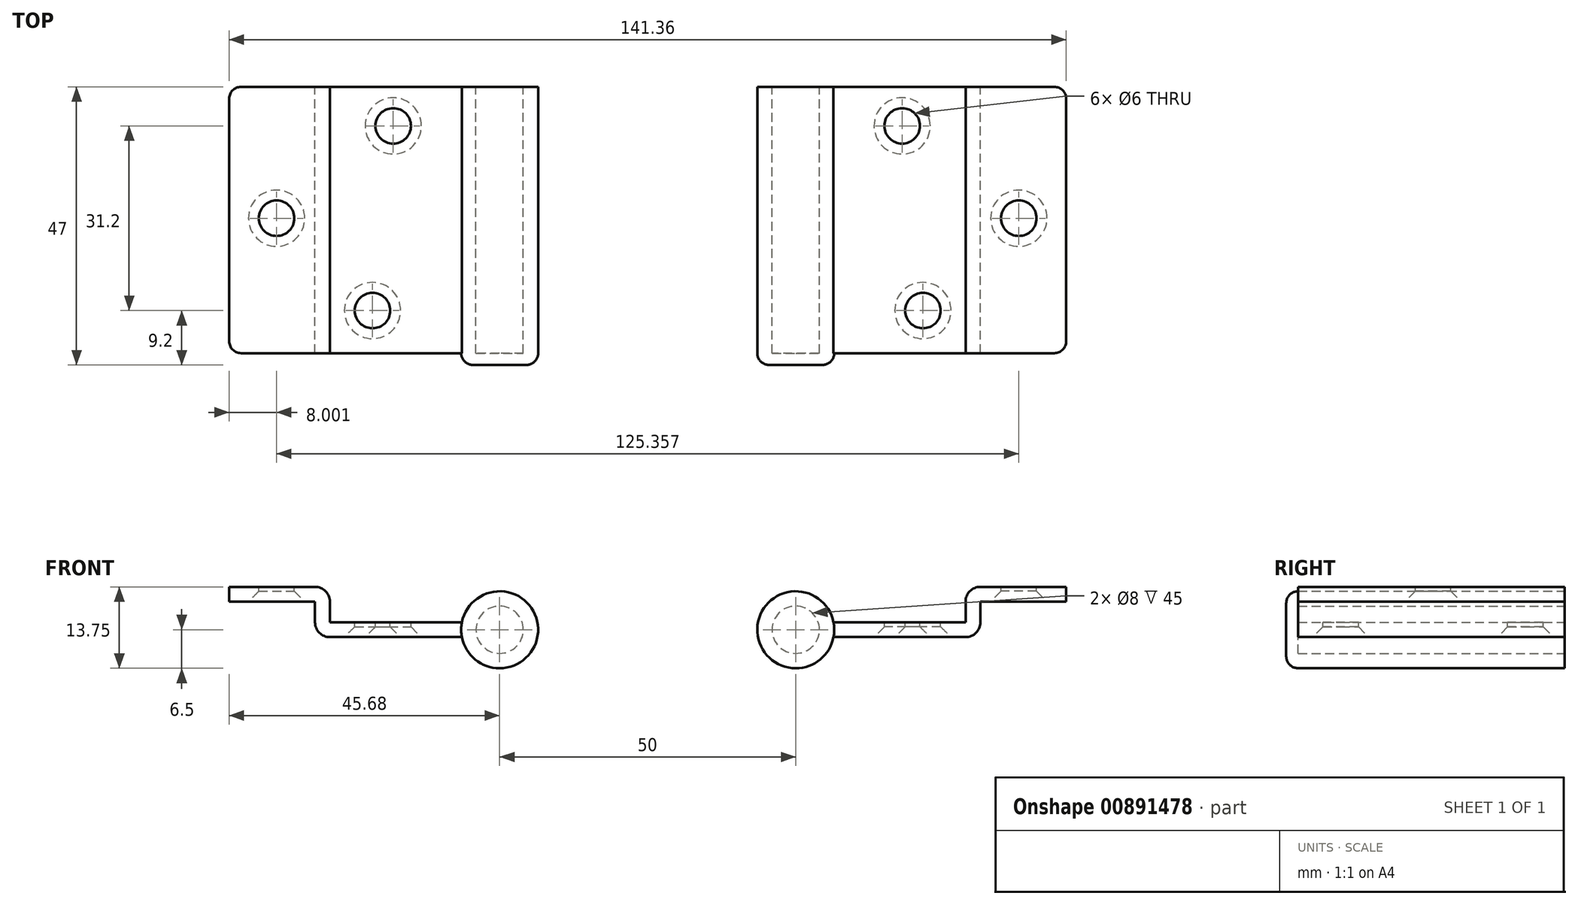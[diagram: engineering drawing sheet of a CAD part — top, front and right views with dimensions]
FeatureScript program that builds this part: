
annotation { "Feature Type Name" : "Feature", "Feature Type Description" : "" }
export const myFeature = defineFeature(function(context is Context, id is Id, definition is map)
    precondition{}
    {
        {
            var Q0;
            Q0=qCreatedBy(makeId("Front.planeOp"),FACE);
            var sketch = newSketch(context, id + "F0", { "sketchPlane" : qUnion([Q0])});
            skArc(sketch, "E0", {"start": v(6.38, 1.25) * mm, "mid": v(-6.5, 0) * mm, "end": v(6.38, -1.25) * mm});
            skLineSegment(sketch, "E1", {"start": v(6.38, 1.25) * mm, "end": v(28.68, 1.25) * mm});
            skLineSegment(sketch, "E2", {"start": v(28.68, 7.25) * mm, "end": v(45.68, 7.25) * mm});
            skLineSegment(sketch, "E3", {"start": v(45.68, 7.25) * mm, "end": v(45.68, 4.75) * mm});
            skLineSegment(sketch, "E4", {"start": v(45.68, 4.75) * mm, "end": v(31.18, 4.75) * mm});
            skLineSegment(sketch, "E5", {"start": v(31.18, -1.25) * mm, "end": v(6.38, -1.25) * mm});
            skLineSegment(sketch, "E6", {"start": v(31.18, 4.75) * mm, "end": v(31.18, -1.25) * mm});
            skLineSegment(sketch, "E7", {"start": v(28.68, 7.25) * mm, "end": v(28.68, 1.25) * mm});
            skCircle(sketch, "E8", {"center": v(0, 0) * mm, "radius": 4 * mm});
            skSolve(sketch);
        }
        {
            var Q0;
            Q0=makeQuery(id+"F0.imprint","IMPRINT",FACE,{"disambiguationData":[TD([[makeQuery(id+"F0.imprint","IMPRINT",EDGE,{"derivedFrom":sQuery(id+"F0.wireOp",EDGE,"E0")}),1.0]])]});
            extrude(context, id + "F1", {"entities" : qUnion([Q0]), "depth" : 45 * mm, "offsetDistance" : 25 * mm});
        }
        {
            var Q0;
            Q0=makeQuery(id+"F1.opExtrude","CAP_EDGE",EDGE,{"disambiguationData":[OSD([sQuery(id+"F0.wireOp",EDGE,"E3")])],"isStart":false});
            var Q1;
            Q1=makeQuery(id+"F1.opExtrude","CAP_EDGE",EDGE,{"disambiguationData":[OSD([sQuery(id+"F0.wireOp",EDGE,"E3")])],"isStart":true});
            fillet(context, id + "F2", {"entities" : qUnion([Q0, Q1]), "radius" : 2 * mm, "tangentPropagation" : true, "allowEdgeOverflow" : false});
        }
        {
            var Q0;
            Q0=makeQuery(id+"F1.opExtrude","SWEPT_EDGE",EDGE,{"disambiguationData":[OSD([sQuery(id+"F0.wireOp",EDGE,"E5"),sQuery(id+"F0.wireOp",EDGE,"E6")])]});
            var Q1;
            Q1=makeQuery(id+"F1.opExtrude","SWEPT_EDGE",EDGE,{"disambiguationData":[OSD([sQuery(id+"F0.wireOp",EDGE,"E2"),sQuery(id+"F0.wireOp",EDGE,"E7")])]});
            fillet(context, id + "F3", {"entities" : qUnion([Q0, Q1]), "radius" : 2.5 * mm, "tangentPropagation" : true, "allowEdgeOverflow" : false});
        }
        {
            var Q0;
            Q0=makeQuery(id+"F1.opExtrude","SWEPT_FACE",FACE,{"disambiguationData":[OSD([sQuery(id+"F0.wireOp",EDGE,"E5")])]});
            var sketch = newSketch(context, id + "F4", { "sketchPlane" : qUnion([Q0])});
            skPoint(sketch, "E9", {"position": v(17.98, 6.6) * mm});
            skPoint(sketch, "E10", {"position": v(21.48, 37.8) * mm});
            skSolve(sketch);
        }
        {
            var Q0;
            Q0=sQuery(id+"F4.wireOp",VERTEX,"E9");
            var Q1;
            Q1=sQuery(id+"F4.wireOp",VERTEX,"E10");
            var Q2;
            Q2=sQuery(id+"F1gnd5VNBVrkXNz_1.wireOp",VERTEX,"af38a646-69fc-4794-a32b-26258d2a7c5d");
            var Q3;
            Q3=makeQuery(id+"F1.opExtrude","SWEPT_BODY",BODY,{"disambiguationData":[OSD([sQuery(id+"F0.wireOp",EDGE,"E0"),sQuery(id+"F0.wireOp",EDGE,"E1"),sQuery(id+"F0.wireOp",EDGE,"WSlHtf5i-U6j4-Ynl4-FoHb-XjoWY4hGSOt6"),sQuery(id+"F0.wireOp",EDGE,"E2"),sQuery(id+"F0.wireOp",EDGE,"E3"),sQuery(id+"F0.wireOp",EDGE,"E4"),sQuery(id+"F0.wireOp",EDGE,"E5"),sQuery(id+"F0.wireOp",EDGE,"dJLKLTg6-jbDR-ftkV-erEf-zidkdKnkohMK"),sQuery(id+"F0.wireOp",EDGE,"M6QVCp6i-pHj4-OTcd-NfKp-MZP8uRFXvbLj"),sQuery(id+"F0.wireOp",EDGE,"RtBS60rh-hvOl-1zH0-KM05-FjQfmGGDyUj7")])]});
            hole(context, id + "F5", {"style" : HoleStyle.C_SINK, "endStyle" : HoleEndStyle.THROUGH, "standardTappedOrClearance" : lookupTablePath({ "standard" : "ISO", "size" : "6", "type" : "Drilled" }), "standardBlindInLast" : lookupTablePath({ "standard" : "ISO", "size" : "6", "type" : "Drilled" }), "holeDiameter" : 6 * mm, "cSinkDiameter" : 9.5 * mm, "cSinkAngle" : 90 * degree, "majorDiameter" : 5 * mm, "isTappedThrough" : true, "tappedDepth" : 12 * mm, "tapClearance" : 3, "startFromSketch" : true, "locations" : qUnion([Q0, Q1, Q2]), "scope" : qUnion([Q3])});
        }
        {
            var Q0;
            Q0=makeQuery(id+"F1.opExtrude","CAP_FACE",FACE,{"disambiguationData":[OSD([sQuery(id+"F0.wireOp",EDGE,"E0"),sQuery(id+"F0.wireOp",EDGE,"E1"),sQuery(id+"F0.wireOp",EDGE,"WSlHtf5i-U6j4-Ynl4-FoHb-XjoWY4hGSOt6"),sQuery(id+"F0.wireOp",EDGE,"E2"),sQuery(id+"F0.wireOp",EDGE,"E3"),sQuery(id+"F0.wireOp",EDGE,"E4"),sQuery(id+"F0.wireOp",EDGE,"E5"),sQuery(id+"F0.wireOp",EDGE,"dJLKLTg6-jbDR-ftkV-erEf-zidkdKnkohMK"),sQuery(id+"F0.wireOp",EDGE,"M6QVCp6i-pHj4-OTcd-NfKp-MZP8uRFXvbLj"),sQuery(id+"F0.wireOp",EDGE,"RtBS60rh-hvOl-1zH0-KM05-FjQfmGGDyUj7")])],"isStart":false});
            var sketch = newSketch(context, id + "F6", { "sketchPlane" : qUnion([Q0])});
            skCircle(sketch, "E11", {"center": v(0, 0) * mm, "radius": 6.5 * mm});
            skSolve(sketch);
        }
        {
            var Q0;
            Q0=qSketchRegion(id+"F6",true);
            extrude(context, id + "F7", {"entities" : qUnion([Q0]), "operationType" : NewBodyOperationType.ADD, "depth" : 2 * mm, "offsetDistance" : 25 * mm});
        }
        {
            var Q0;
            Q0=makeQuery(id+"F7.opExtrude","CAP_EDGE",EDGE,{"disambiguationData":[OSD([sQuery(id+"F6.wireOp",EDGE,"E11")])],"isStart":false});
            fillet(context, id + "F8", {"entities" : qUnion([Q0]), "radius" : 2 * mm, "tangentPropagation" : true, "allowEdgeOverflow" : false});
        }
        {
            var Q0;
            Q0=makeQuery(id+"F1.opExtrude","SWEPT_FACE",FACE,{"disambiguationData":[OSD([sQuery(id+"F0.wireOp",EDGE,"E4")])]});
            var sketch = newSketch(context, id + "F9", { "sketchPlane" : qUnion([Q0])});
            skPoint(sketch, "E12", {"position": v(37.68, 22.2) * mm});
            skLineSegment(sketch, "E13.bottom", {"start": v(28.68, 27.7) * mm, "end": v(33.68, 27.7) * mm});
            skLineSegment(sketch, "E13.top", {"start": v(28.68, 16.7) * mm, "end": v(33.68, 16.7) * mm});
            skLineSegment(sketch, "E13.left", {"start": v(28.68, 27.7) * mm, "end": v(28.68, 16.7) * mm});
            skLineSegment(sketch, "E13.right", {"start": v(33.68, 27.7) * mm, "end": v(33.68, 16.7) * mm});
            skPoint(sketch, "E13.middle", {"position": v(31.18, 22.2) * mm});
            skPoint(sketch, "E13.middle.positionSnap0", {"position": v(31.18, 22.5) * mm});
            skPoint(sketch, "E13.centerSnap0", {"position": v(31.18, 22.5) * mm});
            skSolve(sketch);
        }
        {
            var Q0;
            Q0=sQuery(id+"F9.wireOp",VERTEX,"E12");
            var Q1;
            Q1=makeQuery(id+"F1.opExtrude","SWEPT_BODY",BODY,{"disambiguationData":[OSD([sQuery(id+"F0.wireOp",EDGE,"E0"),sQuery(id+"F0.wireOp",EDGE,"E1"),sQuery(id+"F0.wireOp",EDGE,"E2"),sQuery(id+"F0.wireOp",EDGE,"E3"),sQuery(id+"F0.wireOp",EDGE,"E4"),sQuery(id+"F0.wireOp",EDGE,"E5"),sQuery(id+"F0.wireOp",EDGE,"E6"),sQuery(id+"F0.wireOp",EDGE,"E7")])]});
            hole(context, id + "F10", {"style" : HoleStyle.C_SINK, "endStyle" : HoleEndStyle.THROUGH, "standardTappedOrClearance" : lookupTablePath({ "standard" : "ISO", "size" : "6", "type" : "Drilled" }), "standardBlindInLast" : lookupTablePath({ "standard" : "ISO", "size" : "6", "type" : "Drilled" }), "holeDiameter" : 6 * mm, "cSinkDiameter" : 9.5 * mm, "cSinkAngle" : 90 * degree, "majorDiameter" : 5 * mm, "isTappedThrough" : true, "tappedDepth" : 12 * mm, "tapClearance" : 3, "startFromSketch" : true, "locations" : qUnion([Q0]), "scope" : qUnion([Q1])});
        }
        {
            var Q0;
            Q0=qCreatedBy(makeId("Right.planeOp"),FACE);
            cPlane(context, id + "F11", {"entities" : qUnion([Q0]), "cplaneType" : CPlaneType.OFFSET, "offset" : 25 * mm, "oppositeDirection" : true, "width" : 150 * mm, "height" : 150 * mm});
        }
        {
            var Q0;
            Q0=makeQuery(id+"F1.opExtrude","SWEPT_BODY",BODY,{"disambiguationData":[OSD([sQuery(id+"F0.wireOp",EDGE,"E0"),sQuery(id+"F0.wireOp",EDGE,"E1"),sQuery(id+"F0.wireOp",EDGE,"E2"),sQuery(id+"F0.wireOp",EDGE,"E3"),sQuery(id+"F0.wireOp",EDGE,"E4"),sQuery(id+"F0.wireOp",EDGE,"E5"),sQuery(id+"F0.wireOp",EDGE,"E6"),sQuery(id+"F0.wireOp",EDGE,"E7"),sQuery(id+"F0.wireOp",EDGE,"E8")])]});
            var Q1;
            Q1=qCreatedBy(id+"F11.planeOp",FACE);
            mirror(context, id + "F12", {"entities" : qUnion([Q0]), "mirrorPlane" : qUnion([Q1])});
        }
    });
